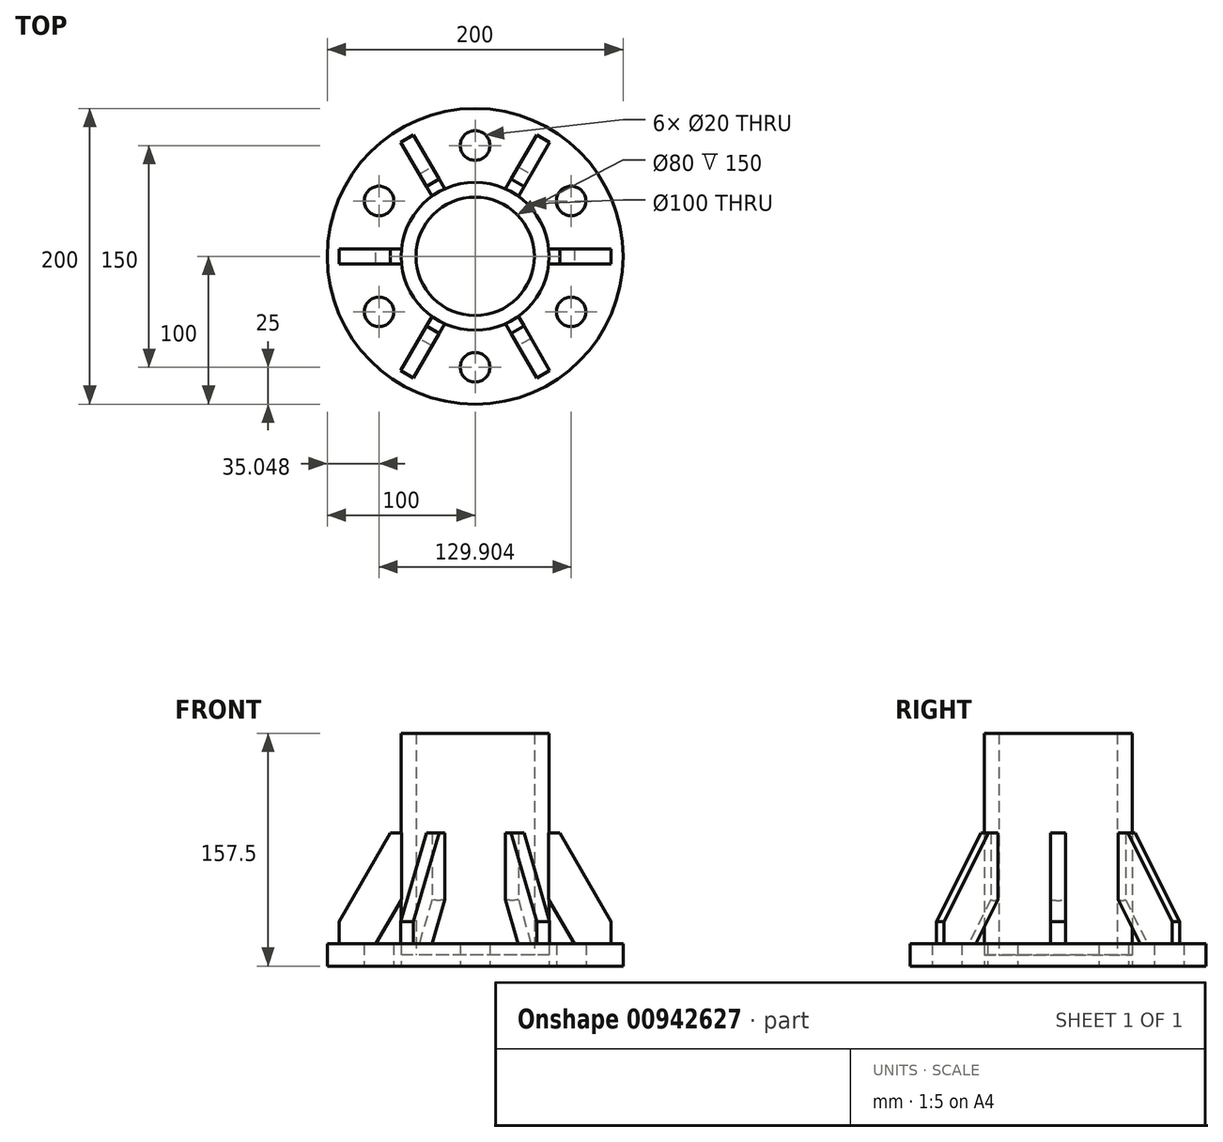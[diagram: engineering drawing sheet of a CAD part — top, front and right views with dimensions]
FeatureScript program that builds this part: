
annotation { "Feature Type Name" : "Feature", "Feature Type Description" : "" }
export const myFeature = defineFeature(function(context is Context, id is Id, definition is map)
    precondition{}
    {
        {
            var Q0;
            Q0=qCreatedBy(makeId("Top.planeOp"),FACE);
            var sketch = newSketch(context, id + "F0", { "sketchPlane" : qUnion([Q0])});
            skCircle(sketch, "E0", {"center": v(0, 0) * mm, "radius": 100 * mm});
            skCircle(sketch, "E1", {"center": v(0, 0) * mm, "radius": 50 * mm});
            skCircle(sketch, "E2", {"center": v(0, 0) * mm, "radius": 40 * mm});
            skCircle(sketch, "E3", {"center": v(0, 75) * mm, "radius": 10 * mm});
            skCircle(sketch, "E4.1.0", {"center": v(-64.95, 37.5) * mm, "radius": 10 * mm});
            skCircle(sketch, "E4.2.0", {"center": v(-64.95, -37.5) * mm, "radius": 10 * mm});
            skCircle(sketch, "E4.3.0", {"center": v(0, -75) * mm, "radius": 10 * mm});
            skCircle(sketch, "E4.4.0", {"center": v(64.95, -37.5) * mm, "radius": 10 * mm});
            skCircle(sketch, "E4.5.0", {"center": v(64.95, 37.5) * mm, "radius": 10 * mm});
            skSolve(sketch);
        }
        {
            var Q0;
            Q0=makeQuery(id+"F0.imprint","IMPRINT",FACE,{"disambiguationData":[TD([[makeQuery(id+"F0.imprint","IMPRINT",EDGE,{"derivedFrom":sQuery(id+"F0.wireOp",EDGE,"E0")}),1.0]])]});
            extrude(context, id + "F1", {"entities" : qUnion([Q0]), "depth" : 15 * mm, "offsetDistance" : 25 * mm});
        }
        {
            var Q0;
            Q0=makeQuery(id+"F0.imprint","IMPRINT",FACE,{"disambiguationData":[TD([[makeQuery(id+"F0.imprint","IMPRINT",EDGE,{"derivedFrom":sQuery(id+"F0.wireOp",EDGE,"E1")}),1.0]])]});
            extrude(context, id + "F2", {"entities" : qUnion([Q0]), "depth" : 157.5 * mm, "offsetDistance" : 7.5 * mm, "hasSecondDirection" : true, "secondDirectionOppositeDirection" : true, "secondDirectionDepth" : -7.5 * mm});
        }
        {
            var Q0;
            Q0=qCreatedBy(makeId("Front.planeOp"),FACE);
            var sketch = newSketch(context, id + "F3", { "sketchPlane" : qUnion([Q0])});
            skLineSegment(sketch, "E5", {"start": v(-92, 15) * mm, "end": v(-92, 30) * mm});
            skLineSegment(sketch, "E6", {"start": v(-92, 30) * mm, "end": v(-57.36, 90) * mm});
            skLineSegment(sketch, "E7", {"start": v(-57.36, 90) * mm, "end": v(-48, 90) * mm});
            skLineSegment(sketch, "E8", {"start": v(-48, 90) * mm, "end": v(-48, 47.9) * mm});
            skLineSegment(sketch, "E9", {"start": v(-48, 47.9) * mm, "end": v(-67, 15) * mm});
            skLineSegment(sketch, "E10", {"start": v(-67, 15) * mm, "end": v(-92, 15) * mm});
            skSolve(sketch);
        }
        {
            var Q0;
            Q0=makeQuery(id+"F3.imprint","IMPRINT",FACE,{"disambiguationData":[TD([[makeQuery(id+"F3.imprint","IMPRINT",EDGE,{"derivedFrom":sQuery(id+"F3.wireOp",EDGE,"E5")}),-1.0]])]});
            extrude(context, id + "F4", {"entities" : qUnion([Q0]), "endBound" : BoundingType.SYMMETRIC, "depth" : 10 * mm, "offsetDistance" : 25 * mm});
        }
        {
            var Q0;
            Q0=makeQuery(id+"F2.opExtrude","SWEPT_BODY",BODY,{"disambiguationData":[OSD([sQuery(id+"F0.wireOp",EDGE,"E1"),sQuery(id+"F0.wireOp",EDGE,"E2")])]});
            var Q1;
            Q1=makeQuery(id+"F4.opExtrude","SWEPT_BODY",BODY,{"disambiguationData":[OSD([sQuery(id+"F3.wireOp",EDGE,"E5"),sQuery(id+"F3.wireOp",EDGE,"E6"),sQuery(id+"F3.wireOp",EDGE,"E7"),sQuery(id+"F3.wireOp",EDGE,"E8"),sQuery(id+"F3.wireOp",EDGE,"E9"),sQuery(id+"F3.wireOp",EDGE,"E10")])]});
            booleanBodies(context, id + "F5", {"operationType" : BooleanOperationType.SUBTRACTION, "tools" : qUnion([Q0]), "targets" : qUnion([Q1]), "keepTools" : true});
        }
        {
            var Q0;
            Q0=makeQuery(id+"F4.opExtrude","SWEPT_BODY",BODY,{"disambiguationData":[OSD([sQuery(id+"F3.wireOp",EDGE,"E5"),sQuery(id+"F3.wireOp",EDGE,"E6"),sQuery(id+"F3.wireOp",EDGE,"E7"),sQuery(id+"F3.wireOp",EDGE,"E8"),sQuery(id+"F3.wireOp",EDGE,"E9"),sQuery(id+"F3.wireOp",EDGE,"E10")])]});
            var Q1;
            Q1=makeQuery(id+"F2.opExtrude","CAP_EDGE",EDGE,{"disambiguationData":[OSD([sQuery(id+"F0.wireOp",EDGE,"E2")])],"isStart":false});
            circularPattern(context, id + "F6", {"entities" : qUnion([Q0]), "axis" : qUnion([Q1]), "angle" : 360 * degree, "instanceCount" : 6, "equalSpace" : true});
        }
    });
